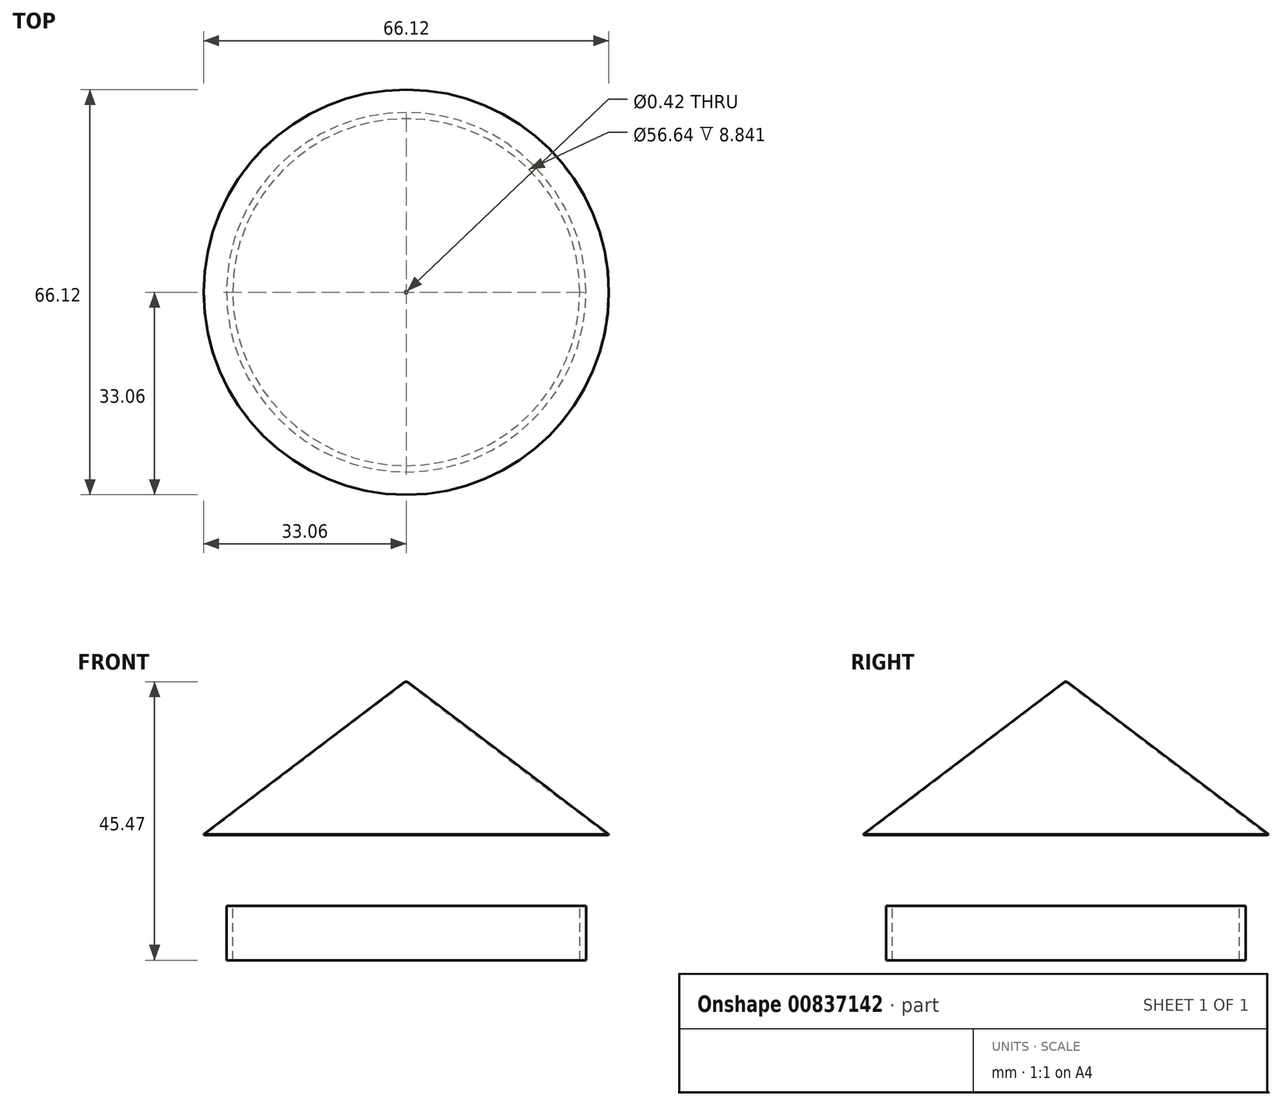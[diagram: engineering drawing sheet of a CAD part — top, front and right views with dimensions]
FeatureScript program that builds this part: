
annotation { "Feature Type Name" : "Feature", "Feature Type Description" : "" }
export const myFeature = defineFeature(function(context is Context, id is Id, definition is map)
    precondition{}
    {
        {
            var Q0;
            Q0=qCreatedBy(makeId("Front.planeOp"),FACE);
            var sketch = newSketch(context, id + "F0", { "sketchPlane" : qUnion([Q0])});
            skLineSegment(sketch, "E0.bottom", {"start": v(-30.23, 22.43) * mm, "end": v(-28.45, 22.43) * mm});
            skLineSegment(sketch, "E1", {"start": v(0, 45.63) * mm, "end": v(-33.06, 20.56) * mm});
            skLineSegment(sketch, "E2", {"start": v(-33.06, 20.56) * mm, "end": v(-32.97, 20.42) * mm});
            skLineSegment(sketch, "E3", {"start": v(-32.97, 20.42) * mm, "end": v(0, 45.42) * mm});
            skCircle(sketch, "E4", {"center": v(0, 45.63) * mm, "radius": 0.2 * mm});
            skLineSegment(sketch, "E5.bottom", {"start": v(-0.2, 45.63) * mm, "end": v(0, 45.63) * mm});
            skLineSegment(sketch, "E5.top", {"start": v(-0.2, 0) * mm, "end": v(0, 0) * mm});
            skLineSegment(sketch, "E5.left", {"start": v(-0.2, 45.63) * mm, "end": v(-0.2, 0) * mm});
            skLineSegment(sketch, "E5.right", {"start": v(0, 45.63) * mm, "end": v(0, 0) * mm});
            skPoint(sketch, "E6.oppositeSnap0", {"position": v(-29.34, 22.43) * mm});
            skLineSegment(sketch, "E6.bottom", {"start": v(-28.32, 0) * mm, "end": v(-29.34, 0) * mm});
            skLineSegment(sketch, "E6.top", {"start": v(-28.32, 8.84) * mm, "end": v(-29.34, 8.84) * mm});
            skLineSegment(sketch, "E6.left", {"start": v(-28.32, 0) * mm, "end": v(-28.32, 8.84) * mm});
            skLineSegment(sketch, "E6.right", {"start": v(-29.34, 0) * mm, "end": v(-29.34, 8.84) * mm});
            skSolve(sketch);
        }
        {
            var Q0;
            {var subQ0=sQuery(id+"F0.wireOp",EDGE,"E2");Q0=makeQuery(id+"F0.imprint","IMPRINT",FACE,{"disambiguationData":[TD([[makeQuery(id+"F0.imprint","IMPRINT",EDGE,{"derivedFrom":subQ0}),1.0]])]});}
            var Q1;
            Q1=makeQuery(id+"F0.imprint","IMPRINT",FACE,{"disambiguationData":[TD([[makeQuery(id+"F0.imprint","IMPRINT",EDGE,{"derivedFrom":sQuery(id+"F0.wireOp",EDGE,"E6.bottom")}),-1.0]])]});
            var Q2;
            Q2=sQuery(id+"F0.wireOp",EDGE,"E5.right");
            revolve(context, id + "F1", {"surfaceOperationType" : NewSurfaceOperationType.NEW, "entities" : qUnion([Q0, Q1]), "axis" : qUnion([Q2]), "revolveType" : RevolveType.FULL});
        }
    });
